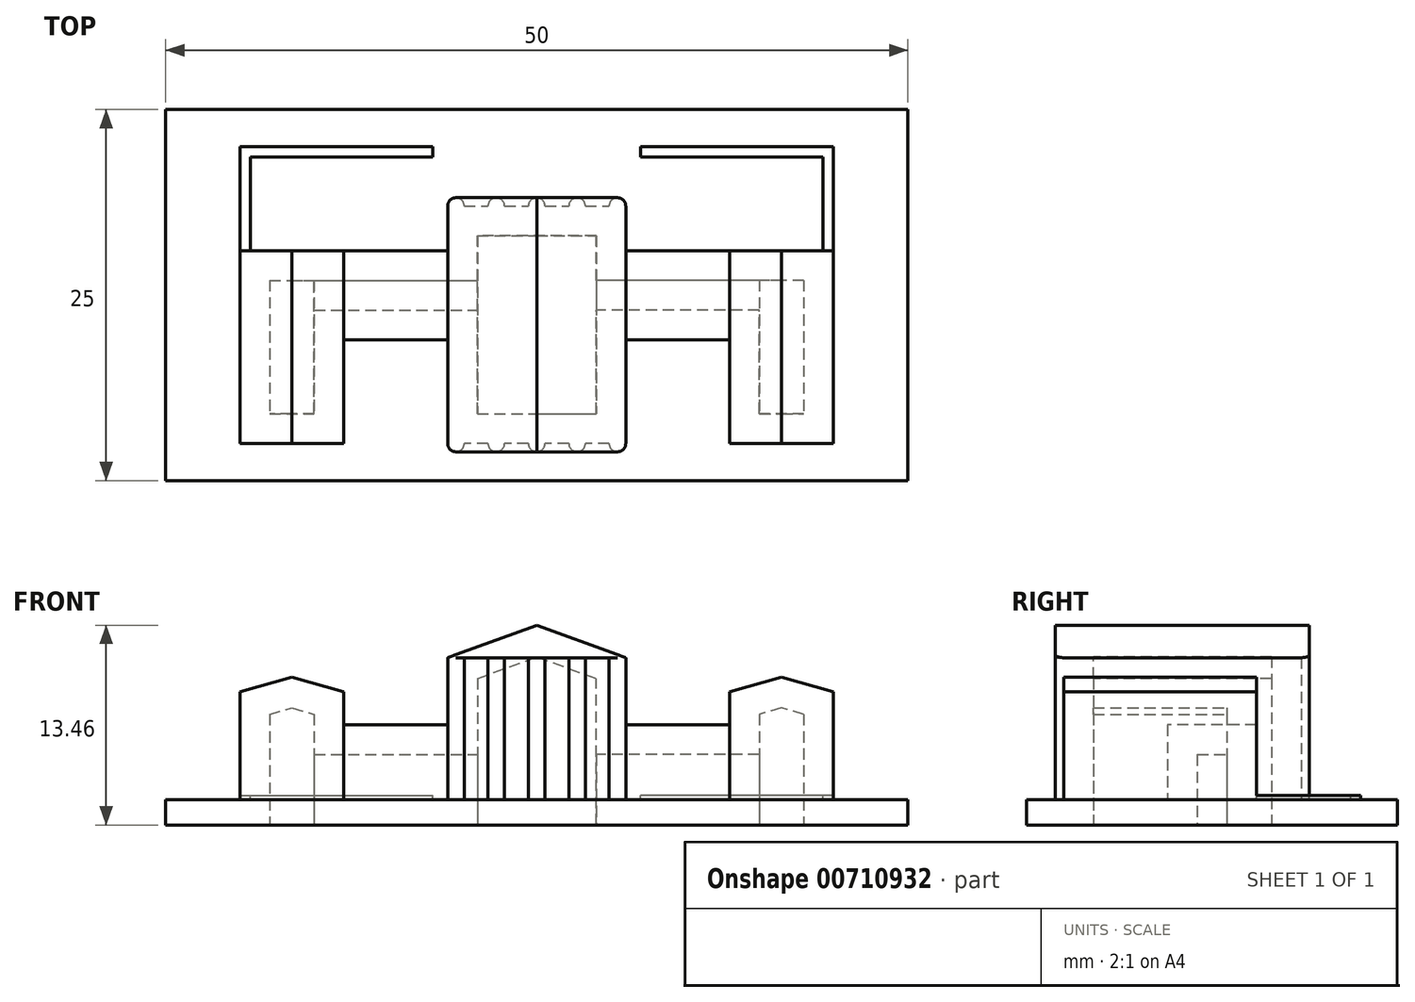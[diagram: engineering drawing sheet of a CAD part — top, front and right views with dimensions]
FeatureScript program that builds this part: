
annotation { "Feature Type Name" : "Feature", "Feature Type Description" : "" }
export const myFeature = defineFeature(function(context is Context, id is Id, definition is map)
    precondition{}
    {
        {
            var Q0;
            Q0=qCreatedBy(makeId("Top.planeOp"),FACE);
            var sketch = newSketch(context, id + "F0", { "sketchPlane" : qUnion([Q0])});
            skLineSegment(sketch, "E0.bottom", {"start": v(-25, 12.5) * mm, "end": v(25, 12.5) * mm});
            skLineSegment(sketch, "E0.top", {"start": v(-25, -12.5) * mm, "end": v(25, -12.5) * mm});
            skLineSegment(sketch, "E0.left", {"start": v(-25, 12.5) * mm, "end": v(-25, -12.5) * mm});
            skLineSegment(sketch, "E0.right", {"start": v(25, 12.5) * mm, "end": v(25, -12.5) * mm});
            skSolve(sketch);
        }
        {
            var Q0;
            Q0=makeQuery(id+"F0.imprint","IMPRINT",FACE,{"disambiguationData":[TD([[makeQuery(id+"F0.imprint","IMPRINT",EDGE,{"derivedFrom":sQuery(id+"F0.wireOp",EDGE,"E0.bottom")}),-1.0]])]});
            var sketch = newSketch(context, id + "F1", { "sketchPlane" : qUnion([Q0])});
            skLineSegment(sketch, "E1", {"start": v(-20, 3) * mm, "end": v(-20, -10) * mm});
            skLineSegment(sketch, "E2", {"start": v(-20, -10) * mm, "end": v(-13, -10) * mm});
            skLineSegment(sketch, "E3", {"start": v(-13, -10) * mm, "end": v(-13, -3) * mm});
            skLineSegment(sketch, "E4", {"start": v(-13, -3) * mm, "end": v(-6, -3) * mm});
            skLineSegment(sketch, "E5", {"start": v(-6, -3) * mm, "end": v(-6, -10) * mm});
            skLineSegment(sketch, "E6", {"start": v(-6, -10) * mm, "end": v(0, -10) * mm});
            skLineSegment(sketch, "E7", {"start": v(-20, 3) * mm, "end": v(-6, 3) * mm});
            skLineSegment(sketch, "E8", {"start": v(-6, 3) * mm, "end": v(-6, 6) * mm});
            skLineSegment(sketch, "E9", {"start": v(-6, 6) * mm, "end": v(0, 6) * mm});
            skLineSegment(sketch, "E10.MirrorCS", {"start": v(20, 3) * mm, "end": v(20, -10) * mm});
            skLineSegment(sketch, "E11.MirrorCS", {"start": v(20, -10) * mm, "end": v(13, -10) * mm});
            skLineSegment(sketch, "E12.MirrorCS", {"start": v(13, -10) * mm, "end": v(13, -3) * mm});
            skLineSegment(sketch, "E13.MirrorCS", {"start": v(13, -3) * mm, "end": v(6, -3) * mm});
            skLineSegment(sketch, "E14.MirrorCS", {"start": v(6, 6) * mm, "end": v(0, 6) * mm});
            skLineSegment(sketch, "E15.MirrorCS", {"start": v(6, -3) * mm, "end": v(6, -10) * mm});
            skLineSegment(sketch, "E16.MirrorCS", {"start": v(6, -10) * mm, "end": v(0, -10) * mm});
            skLineSegment(sketch, "E17.MirrorCS", {"start": v(20, 3) * mm, "end": v(6, 3) * mm});
            skLineSegment(sketch, "E18.MirrorCS", {"start": v(6, 3) * mm, "end": v(6, 6) * mm});
            skSolve(sketch);
        }
        {
            var Q0;
            Q0 = qSketchRegion(id + "F1", true);
            extrude(context, id + "F2", {"entities" : qUnion([Q0]), "depth" : (3 * 3 * .56) * mm, "offsetDistance" : 25 * mm});
        }
        {
            var Q0;
            Q0=makeQuery(id+"F2.opExtrude","CAP_FACE",FACE,{"disambiguationData":[OSD([sQuery(id+"F1.wireOp",EDGE,"E1"),sQuery(id+"F1.wireOp",EDGE,"E2"),sQuery(id+"F1.wireOp",EDGE,"E3"),sQuery(id+"F1.wireOp",EDGE,"E4"),sQuery(id+"F1.wireOp",EDGE,"E5"),sQuery(id+"F1.wireOp",EDGE,"E6"),sQuery(id+"F1.wireOp",EDGE,"E7"),sQuery(id+"F1.wireOp",EDGE,"E8"),sQuery(id+"F1.wireOp",EDGE,"E9"),sQuery(id+"F1.wireOp",EDGE,"E10.MirrorCS"),sQuery(id+"F1.wireOp",EDGE,"E11.MirrorCS"),sQuery(id+"F1.wireOp",EDGE,"E12.MirrorCS"),sQuery(id+"F1.wireOp",EDGE,"E13.MirrorCS"),sQuery(id+"F1.wireOp",EDGE,"E14.MirrorCS"),sQuery(id+"F1.wireOp",EDGE,"E15.MirrorCS"),sQuery(id+"F1.wireOp",EDGE,"E16.MirrorCS"),sQuery(id+"F1.wireOp",EDGE,"E17.MirrorCS"),sQuery(id+"F1.wireOp",EDGE,"E18.MirrorCS")])],"isStart":false});
            var sketch = newSketch(context, id + "F3", { "sketchPlane" : qUnion([Q0])});
            skLineSegment(sketch, "E19.bottom", {"start": v(20, 3) * mm, "end": v(13, 3) * mm});
            skLineSegment(sketch, "E19.top", {"start": v(20, -10) * mm, "end": v(13, -10) * mm});
            skLineSegment(sketch, "E19.left", {"start": v(20, 3) * mm, "end": v(20, -10) * mm});
            skLineSegment(sketch, "E19.right", {"start": v(13, 3) * mm, "end": v(13, -10) * mm});
            skLineSegment(sketch, "E20.bottom", {"start": v(6, -10) * mm, "end": v(-6, -10) * mm});
            skLineSegment(sketch, "E20.top", {"start": v(6, 6) * mm, "end": v(-6, 6) * mm});
            skLineSegment(sketch, "E20.left", {"start": v(6, -10) * mm, "end": v(6, 6) * mm});
            skLineSegment(sketch, "E20.right", {"start": v(-6, -10) * mm, "end": v(-6, 6) * mm});
            skLineSegment(sketch, "E21.bottom", {"start": v(-20, -10) * mm, "end": v(-13, -10) * mm});
            skLineSegment(sketch, "E21.top", {"start": v(-20, 3) * mm, "end": v(-13, 3) * mm});
            skLineSegment(sketch, "E21.left", {"start": v(-20, -10) * mm, "end": v(-20, 3) * mm});
            skLineSegment(sketch, "E21.right", {"start": v(-13, -10) * mm, "end": v(-13, 3) * mm});
            skSolve(sketch);
        }
        {
            var Q0;
            Q0 = qSketchRegion(id + "F3", true);
            extrude(context, id + "F4", {"entities" : qUnion([Q0]), "operationType" : NewBodyOperationType.ADD, "depth" : (2 * 3 * .56) * mm, "offsetDistance" : 25 * mm});
        }
        {
            var Q0;
            Q0=makeQuery(id+"F4.opExtrude","CAP_EDGE",EDGE,{"disambiguationData":[OSD([sQuery(id+"F3.wireOp",EDGE,"E19.left")])],"isStart":false});
            var Q1;
            Q1=makeQuery(id+"F4.opExtrude","CAP_EDGE",EDGE,{"disambiguationData":[OSD([sQuery(id+"F3.wireOp",EDGE,"E19.right")])],"isStart":false});
            chamfer(context, id + "F5", {"entities" : qUnion([Q0, Q1]), "chamferType" : ChamferType.TWO_OFFSETS, "width1" : 1.12 * mm, "oppositeDirection" : false, "width2" : 4 * mm, "tangentPropagation" : true});
        }
        {
            var Q0;
            Q0=makeQuery(id+"F4.opExtrude","CAP_EDGE",EDGE,{"disambiguationData":[OSD([sQuery(id+"F3.wireOp",EDGE,"E21.right")])],"isStart":false});
            var Q1;
            Q1=makeQuery(id+"F4.opExtrude","CAP_EDGE",EDGE,{"disambiguationData":[OSD([sQuery(id+"F3.wireOp",EDGE,"E21.left")])],"isStart":false});
            chamfer(context, id + "F6", {"entities" : qUnion([Q0, Q1]), "chamferType" : ChamferType.TWO_OFFSETS, "width1" : 4 * mm, "oppositeDirection" : false, "width2" : 1.12 * mm, "tangentPropagation" : true});
        }
        {
            var Q0;
            Q0=makeQuery(id+"F4.opExtrude","CAP_FACE",FACE,{"disambiguationData":[OSD([sQuery(id+"F3.wireOp",EDGE,"E20.bottom"),sQuery(id+"F3.wireOp",EDGE,"E20.top"),sQuery(id+"F3.wireOp",EDGE,"E20.left"),sQuery(id+"F3.wireOp",EDGE,"E20.right")])],"isStart":false});
            var sketch = newSketch(context, id + "F7", { "sketchPlane" : qUnion([Q0])});
            skLineSegment(sketch, "E22.bottom", {"start": v(6, -10) * mm, "end": v(-6, -10) * mm});
            skLineSegment(sketch, "E22.top", {"start": v(6, 6) * mm, "end": v(-6, 6) * mm});
            skLineSegment(sketch, "E22.left", {"start": v(6, -10) * mm, "end": v(6, 6) * mm});
            skLineSegment(sketch, "E22.right", {"start": v(-6, -10) * mm, "end": v(-6, 6) * mm});
            skSolve(sketch);
        }
        {
            var Q0;
            Q0 = qSketchRegion(id + "F7", true);
            extrude(context, id + "F8", {"entities" : qUnion([Q0]), "operationType" : NewBodyOperationType.ADD, "depth" : (2 * 3 * .56) * mm, "offsetDistance" : 25 * mm});
        }
        {
            var Q0;
            Q0=makeQuery(id+"F8.opExtrude","CAP_EDGE",EDGE,{"disambiguationData":[OSD([sQuery(id+"F7.wireOp",EDGE,"E22.left")])],"isStart":false});
            var Q1;
            Q1=makeQuery(id+"F8.opExtrude","CAP_EDGE",EDGE,{"disambiguationData":[OSD([sQuery(id+"F7.wireOp",EDGE,"E22.right")])],"isStart":false});
            chamfer(context, id + "F9", {"entities" : qUnion([Q0, Q1]), "chamferType" : ChamferType.OFFSET_ANGLE, "width" : 6 * mm, "oppositeDirection" : true, "angle" : 20 * degree, "tangentPropagation" : true});
        }
        {
            var Q0;
            Q0=makeQuery(id+"F8.boolean.opBoolean","MERGE",FACE,{"derivedFrom":[makeQuery(id+"F4.boolean.opBoolean","MERGE",FACE,{"derivedFrom":[makeQuery(id+"F2.opExtrude","SWEPT_FACE",FACE,{"disambiguationData":[OSD([sQuery(id+"F1.wireOp",EDGE,"E9"),sQuery(id+"F1.wireOp",EDGE,"E14.MirrorCS")])]}),makeQuery(id+"F4.opExtrude","SWEPT_FACE",FACE,{"disambiguationData":[OSD([sQuery(id+"F3.wireOp",EDGE,"E20.top")])]})]}),makeQuery(id+"F8.opExtrude","SWEPT_FACE",FACE,{"disambiguationData":[OSD([sQuery(id+"F7.wireOp",EDGE,"E22.top")])]})]});
            var sketch = newSketch(context, id + "F10", { "sketchPlane" : qUnion([Q0])});
            skLineSegment(sketch, "E23", {"start": v(-6, 9.58) * mm, "end": v(0, 11.76) * mm});
            skLineSegment(sketch, "E24", {"start": v(0, 11.76) * mm, "end": v(6, 9.58) * mm});
            skLineSegment(sketch, "E25", {"start": v(6, 9.58) * mm, "end": v(-6, 9.58) * mm});
            skLineSegment(sketch, "E26.bottom", {"start": v(-6, 9.58) * mm, "end": v(-4.88, 9.58) * mm});
            skLineSegment(sketch, "E26.top", {"start": v(-6, 0) * mm, "end": v(-4.88, 0) * mm});
            skLineSegment(sketch, "E26.left", {"start": v(-6, 9.58) * mm, "end": v(-6, 0) * mm});
            skLineSegment(sketch, "E26.right", {"start": v(-4.88, 9.58) * mm, "end": v(-4.88, 0) * mm});
            skLineSegment(sketch, "E27.bottom", {"start": v(-3.28, 9.58) * mm, "end": v(-2.16, 9.58) * mm});
            skLineSegment(sketch, "E27.top", {"start": v(-3.28, 0) * mm, "end": v(-2.16, 0) * mm});
            skLineSegment(sketch, "E27.left", {"start": v(-3.28, 9.58) * mm, "end": v(-3.28, 0) * mm});
            skLineSegment(sketch, "E27.right", {"start": v(-2.16, 9.58) * mm, "end": v(-2.16, 0) * mm});
            skLineSegment(sketch, "E28.bottom", {"start": v(-0.56, 9.58) * mm, "end": v(0.56, 9.58) * mm});
            skLineSegment(sketch, "E28.top", {"start": v(-0.56, 0) * mm, "end": v(0.56, 0) * mm});
            skLineSegment(sketch, "E28.left", {"start": v(-0.56, 9.58) * mm, "end": v(-0.56, 0) * mm});
            skLineSegment(sketch, "E28.right", {"start": v(0.56, 9.58) * mm, "end": v(0.56, 0) * mm});
            skLineSegment(sketch, "E29.bottom", {"start": v(2.16, 9.58) * mm, "end": v(3.28, 9.58) * mm});
            skLineSegment(sketch, "E29.top", {"start": v(2.16, 0) * mm, "end": v(3.28, 0) * mm});
            skLineSegment(sketch, "E29.left", {"start": v(2.16, 9.58) * mm, "end": v(2.16, 0) * mm});
            skLineSegment(sketch, "E29.right", {"start": v(3.28, 9.58) * mm, "end": v(3.28, 0) * mm});
            skLineSegment(sketch, "E30.bottom", {"start": v(4.88, 9.58) * mm, "end": v(6, 9.58) * mm});
            skLineSegment(sketch, "E30.top", {"start": v(4.88, 0) * mm, "end": v(6, 0) * mm});
            skLineSegment(sketch, "E30.left", {"start": v(4.88, 9.58) * mm, "end": v(4.88, 0) * mm});
            skLineSegment(sketch, "E30.right", {"start": v(6, 9.58) * mm, "end": v(6, 0) * mm});
            skSolve(sketch);
        }
        {
            var Q0;
            Q0 = qSketchRegion(id + "F10", true);
            extrude(context, id + "F11", {"entities" : qUnion([Q0]), "operationType" : NewBodyOperationType.ADD, "depth" : .56 * mm, "offsetDistance" : 25 * mm});
        }
        {
            var Q0;
            Q0=makeQuery(id+"F11.opExtrude","CAP_EDGE",EDGE,{"disambiguationData":[OSD([sQuery(id+"F10.wireOp",EDGE,"E26.left")])],"isStart":false});
            var Q1;
            Q1=makeQuery(id+"F11.opExtrude","CAP_EDGE",EDGE,{"disambiguationData":[OSD([sQuery(id+"F10.wireOp",EDGE,"E26.right")])],"isStart":false});
            var Q2;
            Q2=makeQuery(id+"F11.opExtrude","CAP_EDGE",EDGE,{"disambiguationData":[OSD([sQuery(id+"F10.wireOp",EDGE,"E27.left")])],"isStart":false});
            var Q3;
            Q3=makeQuery(id+"F11.opExtrude","CAP_EDGE",EDGE,{"disambiguationData":[OSD([sQuery(id+"F10.wireOp",EDGE,"E27.right")])],"isStart":false});
            var Q4;
            Q4=makeQuery(id+"F11.opExtrude","CAP_EDGE",EDGE,{"disambiguationData":[OSD([sQuery(id+"F10.wireOp",EDGE,"E28.left")])],"isStart":false});
            var Q5;
            Q5=makeQuery(id+"F11.opExtrude","CAP_EDGE",EDGE,{"disambiguationData":[OSD([sQuery(id+"F10.wireOp",EDGE,"E28.right")])],"isStart":false});
            var Q6;
            Q6=makeQuery(id+"F11.opExtrude","CAP_EDGE",EDGE,{"disambiguationData":[OSD([sQuery(id+"F10.wireOp",EDGE,"E29.left")])],"isStart":false});
            var Q7;
            Q7=makeQuery(id+"F11.opExtrude","CAP_EDGE",EDGE,{"disambiguationData":[OSD([sQuery(id+"F10.wireOp",EDGE,"E29.right")])],"isStart":false});
            var Q8;
            Q8=makeQuery(id+"F11.opExtrude","CAP_EDGE",EDGE,{"disambiguationData":[OSD([sQuery(id+"F10.wireOp",EDGE,"E30.left")])],"isStart":false});
            var Q9;
            Q9=makeQuery(id+"F11.opExtrude","CAP_EDGE",EDGE,{"disambiguationData":[OSD([sQuery(id+"F10.wireOp",EDGE,"E30.right")])],"isStart":false});
            fillet(context, id + "F12", {"entities" : qUnion([Q0, Q1, Q2, Q3, Q4, Q5, Q6, Q7, Q8, Q9]), "radius" : .56 * mm, "tangentPropagation" : true, "allowEdgeOverflow" : false});
        }
        {
            var Q0;
            Q0=makeQuery(id+"F8.boolean.opBoolean","MERGE",FACE,{"derivedFrom":[makeQuery(id+"F4.boolean.opBoolean","MERGE",FACE,{"derivedFrom":[makeQuery(id+"F2.opExtrude","SWEPT_FACE",FACE,{"disambiguationData":[OSD([sQuery(id+"F1.wireOp",EDGE,"E6"),sQuery(id+"F1.wireOp",EDGE,"E16.MirrorCS")])]}),makeQuery(id+"F4.opExtrude","SWEPT_FACE",FACE,{"disambiguationData":[OSD([sQuery(id+"F3.wireOp",EDGE,"E20.bottom")])]})]}),makeQuery(id+"F8.opExtrude","SWEPT_FACE",FACE,{"disambiguationData":[OSD([sQuery(id+"F7.wireOp",EDGE,"E22.bottom")])]})]});
            var sketch = newSketch(context, id + "F13", { "sketchPlane" : qUnion([Q0])});
            skLineSegment(sketch, "E31", {"start": v(-6, 9.58) * mm, "end": v(0, 11.76) * mm});
            skLineSegment(sketch, "E32", {"start": v(0, 11.76) * mm, "end": v(6, 9.58) * mm});
            skLineSegment(sketch, "E33", {"start": v(6, 9.58) * mm, "end": v(-6, 9.58) * mm});
            skLineSegment(sketch, "E34.bottom", {"start": v(-6, 9.58) * mm, "end": v(-4.88, 9.58) * mm});
            skLineSegment(sketch, "E34.top", {"start": v(-6, 0) * mm, "end": v(-4.88, 0) * mm});
            skLineSegment(sketch, "E34.left", {"start": v(-6, 9.58) * mm, "end": v(-6, 0) * mm});
            skLineSegment(sketch, "E34.right", {"start": v(-4.88, 9.58) * mm, "end": v(-4.88, 0) * mm});
            skLineSegment(sketch, "E35.bottom", {"start": v(-3.28, 9.58) * mm, "end": v(-2.16, 9.58) * mm});
            skLineSegment(sketch, "E35.top", {"start": v(-3.28, 0) * mm, "end": v(-2.16, 0) * mm});
            skLineSegment(sketch, "E35.left", {"start": v(-3.28, 9.58) * mm, "end": v(-3.28, 0) * mm});
            skLineSegment(sketch, "E35.right", {"start": v(-2.16, 9.58) * mm, "end": v(-2.16, 0) * mm});
            skLineSegment(sketch, "E36.bottom", {"start": v(-0.56, 9.58) * mm, "end": v(0.56, 9.58) * mm});
            skLineSegment(sketch, "E36.top", {"start": v(-0.56, 0) * mm, "end": v(0.56, 0) * mm});
            skLineSegment(sketch, "E36.left", {"start": v(-0.56, 9.58) * mm, "end": v(-0.56, 0) * mm});
            skLineSegment(sketch, "E36.right", {"start": v(0.56, 9.58) * mm, "end": v(0.56, 0) * mm});
            skLineSegment(sketch, "E37.bottom", {"start": v(2.16, 9.58) * mm, "end": v(3.28, 9.58) * mm});
            skLineSegment(sketch, "E37.top", {"start": v(2.16, 0) * mm, "end": v(3.28, 0) * mm});
            skLineSegment(sketch, "E37.left", {"start": v(2.16, 9.58) * mm, "end": v(2.16, 0) * mm});
            skLineSegment(sketch, "E37.right", {"start": v(3.28, 9.58) * mm, "end": v(3.28, 0) * mm});
            skLineSegment(sketch, "E38.bottom", {"start": v(4.88, 9.58) * mm, "end": v(6, 9.58) * mm});
            skLineSegment(sketch, "E38.top", {"start": v(4.88, 0) * mm, "end": v(6, 0) * mm});
            skLineSegment(sketch, "E38.left", {"start": v(4.88, 9.58) * mm, "end": v(4.88, 0) * mm});
            skLineSegment(sketch, "E38.right", {"start": v(6, 9.58) * mm, "end": v(6, 0) * mm});
            skSolve(sketch);
        }
        {
            var Q0;
            Q0 = qSketchRegion(id + "F13", true);
            extrude(context, id + "F14", {"entities" : qUnion([Q0]), "operationType" : NewBodyOperationType.ADD, "depth" : .56 * mm, "offsetDistance" : 25 * mm});
        }
        {
            var Q0;
            Q0=makeQuery(id+"F14.opExtrude","CAP_EDGE",EDGE,{"disambiguationData":[OSD([sQuery(id+"F13.wireOp",EDGE,"E34.right")])],"isStart":false});
            var Q1;
            Q1=makeQuery(id+"F14.opExtrude","CAP_EDGE",EDGE,{"disambiguationData":[OSD([sQuery(id+"F13.wireOp",EDGE,"E35.left")])],"isStart":false});
            var Q2;
            Q2=makeQuery(id+"F14.opExtrude","CAP_EDGE",EDGE,{"disambiguationData":[OSD([sQuery(id+"F13.wireOp",EDGE,"E35.right")])],"isStart":false});
            var Q3;
            Q3=makeQuery(id+"F14.opExtrude","CAP_EDGE",EDGE,{"disambiguationData":[OSD([sQuery(id+"F13.wireOp",EDGE,"E34.left")])],"isStart":false});
            var Q4;
            Q4=makeQuery(id+"F14.opExtrude","CAP_EDGE",EDGE,{"disambiguationData":[OSD([sQuery(id+"F13.wireOp",EDGE,"E36.left")])],"isStart":false});
            var Q5;
            Q5=makeQuery(id+"F14.opExtrude","CAP_EDGE",EDGE,{"disambiguationData":[OSD([sQuery(id+"F13.wireOp",EDGE,"E36.right")])],"isStart":false});
            var Q6;
            Q6=makeQuery(id+"F14.opExtrude","CAP_EDGE",EDGE,{"disambiguationData":[OSD([sQuery(id+"F13.wireOp",EDGE,"E37.left")])],"isStart":false});
            var Q7;
            Q7=makeQuery(id+"F14.opExtrude","CAP_EDGE",EDGE,{"disambiguationData":[OSD([sQuery(id+"F13.wireOp",EDGE,"E37.right")])],"isStart":false});
            var Q8;
            Q8=makeQuery(id+"F14.opExtrude","CAP_EDGE",EDGE,{"disambiguationData":[OSD([sQuery(id+"F13.wireOp",EDGE,"E38.left")])],"isStart":false});
            var Q9;
            Q9=makeQuery(id+"F14.opExtrude","CAP_EDGE",EDGE,{"disambiguationData":[OSD([sQuery(id+"F13.wireOp",EDGE,"E38.right")])],"isStart":false});
            fillet(context, id + "F15", {"entities" : qUnion([Q0, Q1, Q2, Q3, Q4, Q5, Q6, Q7, Q8, Q9]), "radius" : .56 * mm, "tangentPropagation" : true, "allowEdgeOverflow" : false});
        }
        {
            var Q0;
            Q0=makeQuery(id+"F0.imprint","IMPRINT",FACE,{"disambiguationData":[TD([[makeQuery(id+"F0.imprint","IMPRINT",EDGE,{"derivedFrom":sQuery(id+"F0.wireOp",EDGE,"E0.bottom")}),-1.0]])]});
            var sketch = newSketch(context, id + "F16", { "sketchPlane" : qUnion([Q0])});
            skLineSegment(sketch, "E39", {"start": v(20, 3) * mm, "end": v(20, 10) * mm});
            skLineSegment(sketch, "E40", {"start": v(20, 10) * mm, "end": v(7, 10) * mm});
            skSolve(sketch);
        }
        {
            var Q0;
            Q0=makeQuery(id+"F4.boolean.opBoolean","MERGE",FACE,{"derivedFrom":[makeQuery(id+"F2.opExtrude","SWEPT_FACE",FACE,{"disambiguationData":[OSD([sQuery(id+"F1.wireOp",EDGE,"E17.MirrorCS")])]}),makeQuery(id+"F4.opExtrude","SWEPT_FACE",FACE,{"disambiguationData":[OSD([sQuery(id+"F3.wireOp",EDGE,"E19.bottom")])]})]});
            var sketch = newSketch(context, id + "F17", { "sketchPlane" : qUnion([Q0])});
            skLineSegment(sketch, "E41.bottom", {"start": v(-20, 0) * mm, "end": v(-19.3, 0) * mm});
            skLineSegment(sketch, "E41.top", {"start": v(-20, 0.3) * mm, "end": v(-19.3, 0.3) * mm});
            skLineSegment(sketch, "E41.left", {"start": v(-20, 0) * mm, "end": v(-20, 0.3) * mm});
            skLineSegment(sketch, "E41.right", {"start": v(-19.3, 0) * mm, "end": v(-19.3, 0.3) * mm});
            skSolve(sketch);
        }
        {
            var Q0;
            Q0=makeQuery(id+"F17.imprint","IMPRINT",FACE,{"disambiguationData":[TD([[makeQuery(id+"F17.imprint","IMPRINT",EDGE,{"derivedFrom":sQuery(id+"F17.wireOp",EDGE,"E41.bottom")}),1.0]])]});
            var Q1;
            Q1=sQuery(id+"F16.wireOp",EDGE,"E39");
            var Q2;
            Q2=sQuery(id+"F16.wireOp",EDGE,"E40");
            sweep(context, id + "F18", {"operationType" : NewBodyOperationType.ADD, "profiles" : qUnion([Q0]), "path" : qUnion([Q1, Q2])});
        }
        {
            var Q0;
            Q0=makeQuery(id+"F2.opExtrude","SWEPT_BODY",BODY,{"disambiguationData":[OSD([sQuery(id+"F1.wireOp",EDGE,"E1"),sQuery(id+"F1.wireOp",EDGE,"E2"),sQuery(id+"F1.wireOp",EDGE,"E3"),sQuery(id+"F1.wireOp",EDGE,"E4"),sQuery(id+"F1.wireOp",EDGE,"E5"),sQuery(id+"F1.wireOp",EDGE,"E6"),sQuery(id+"F1.wireOp",EDGE,"E7"),sQuery(id+"F1.wireOp",EDGE,"E8"),sQuery(id+"F1.wireOp",EDGE,"E9"),sQuery(id+"F1.wireOp",EDGE,"E10.MirrorCS"),sQuery(id+"F1.wireOp",EDGE,"E11.MirrorCS"),sQuery(id+"F1.wireOp",EDGE,"E12.MirrorCS"),sQuery(id+"F1.wireOp",EDGE,"E13.MirrorCS"),sQuery(id+"F1.wireOp",EDGE,"E14.MirrorCS"),sQuery(id+"F1.wireOp",EDGE,"E15.MirrorCS"),sQuery(id+"F1.wireOp",EDGE,"E16.MirrorCS"),sQuery(id+"F1.wireOp",EDGE,"E17.MirrorCS"),sQuery(id+"F1.wireOp",EDGE,"E18.MirrorCS")])]});
            var Q1;
            Q1=qCreatedBy(makeId("Right.planeOp"),FACE);
            mirror(context, id + "F19", {"operationType" : NewBodyOperationType.ADD, "entities" : qUnion([Q0]), "mirrorPlane" : qUnion([Q1])});
        }
        {
            var Q0;
            Q0=makeQuery(id+"F0.imprint","IMPRINT",FACE,{"disambiguationData":[TD([[makeQuery(id+"F0.imprint","IMPRINT",EDGE,{"derivedFrom":sQuery(id+"F0.wireOp",EDGE,"E0.bottom")}),-1.0]])]});
            extrude(context, id + "F20", {"entities" : qUnion([Q0]), "operationType" : NewBodyOperationType.ADD, "oppositeDirection" : true, "depth" : 1.7 * mm, "offsetDistance" : 25 * mm});
        }
        {
            var Q0;
            Q0=makeQuery(id+"F11.boolean.opBoolean","MERGE",FACE,{"derivedFrom":[makeQuery(id+"F2.opExtrude","CAP_FACE",FACE,{"disambiguationData":[OSD([sQuery(id+"F1.wireOp",EDGE,"E1"),sQuery(id+"F1.wireOp",EDGE,"E2"),sQuery(id+"F1.wireOp",EDGE,"E3"),sQuery(id+"F1.wireOp",EDGE,"E4"),sQuery(id+"F1.wireOp",EDGE,"E5"),sQuery(id+"F1.wireOp",EDGE,"E6"),sQuery(id+"F1.wireOp",EDGE,"E7"),sQuery(id+"F1.wireOp",EDGE,"E8"),sQuery(id+"F1.wireOp",EDGE,"E9"),sQuery(id+"F1.wireOp",EDGE,"E10.MirrorCS"),sQuery(id+"F1.wireOp",EDGE,"E11.MirrorCS"),sQuery(id+"F1.wireOp",EDGE,"E12.MirrorCS"),sQuery(id+"F1.wireOp",EDGE,"E13.MirrorCS"),sQuery(id+"F1.wireOp",EDGE,"E14.MirrorCS"),sQuery(id+"F1.wireOp",EDGE,"E15.MirrorCS"),sQuery(id+"F1.wireOp",EDGE,"E16.MirrorCS"),sQuery(id+"F1.wireOp",EDGE,"E17.MirrorCS"),sQuery(id+"F1.wireOp",EDGE,"E18.MirrorCS")])],"isStart":true}),makeQuery(id+"F11.opExtrude","SWEPT_FACE",FACE,{"disambiguationData":[OSD([sQuery(id+"F10.wireOp",EDGE,"E26.top")])]}),makeQuery(id+"F11.opExtrude","SWEPT_FACE",FACE,{"disambiguationData":[OSD([sQuery(id+"F10.wireOp",EDGE,"E27.top")])]}),makeQuery(id+"F11.opExtrude","SWEPT_FACE",FACE,{"disambiguationData":[OSD([sQuery(id+"F10.wireOp",EDGE,"E28.top")])]}),makeQuery(id+"F11.opExtrude","SWEPT_FACE",FACE,{"disambiguationData":[OSD([sQuery(id+"F10.wireOp",EDGE,"E29.top")])]}),makeQuery(id+"F11.opExtrude","SWEPT_FACE",FACE,{"disambiguationData":[OSD([sQuery(id+"F10.wireOp",EDGE,"E30.top")])]})]});
            var Q1;
            Q1=makeQuery(id+"F20.opExtrude","CAP_FACE",FACE,{"disambiguationData":[OSD([sQuery(id+"F0.wireOp",EDGE,"E0.bottom"),sQuery(id+"F0.wireOp",EDGE,"E0.top"),sQuery(id+"F0.wireOp",EDGE,"E0.left"),sQuery(id+"F0.wireOp",EDGE,"E0.right")])],"isStart":false});
            shell(context, id + "F21", {"entities" : qUnion([Q0, Q1]), "thickness" : 2 * mm});
        }
    });
